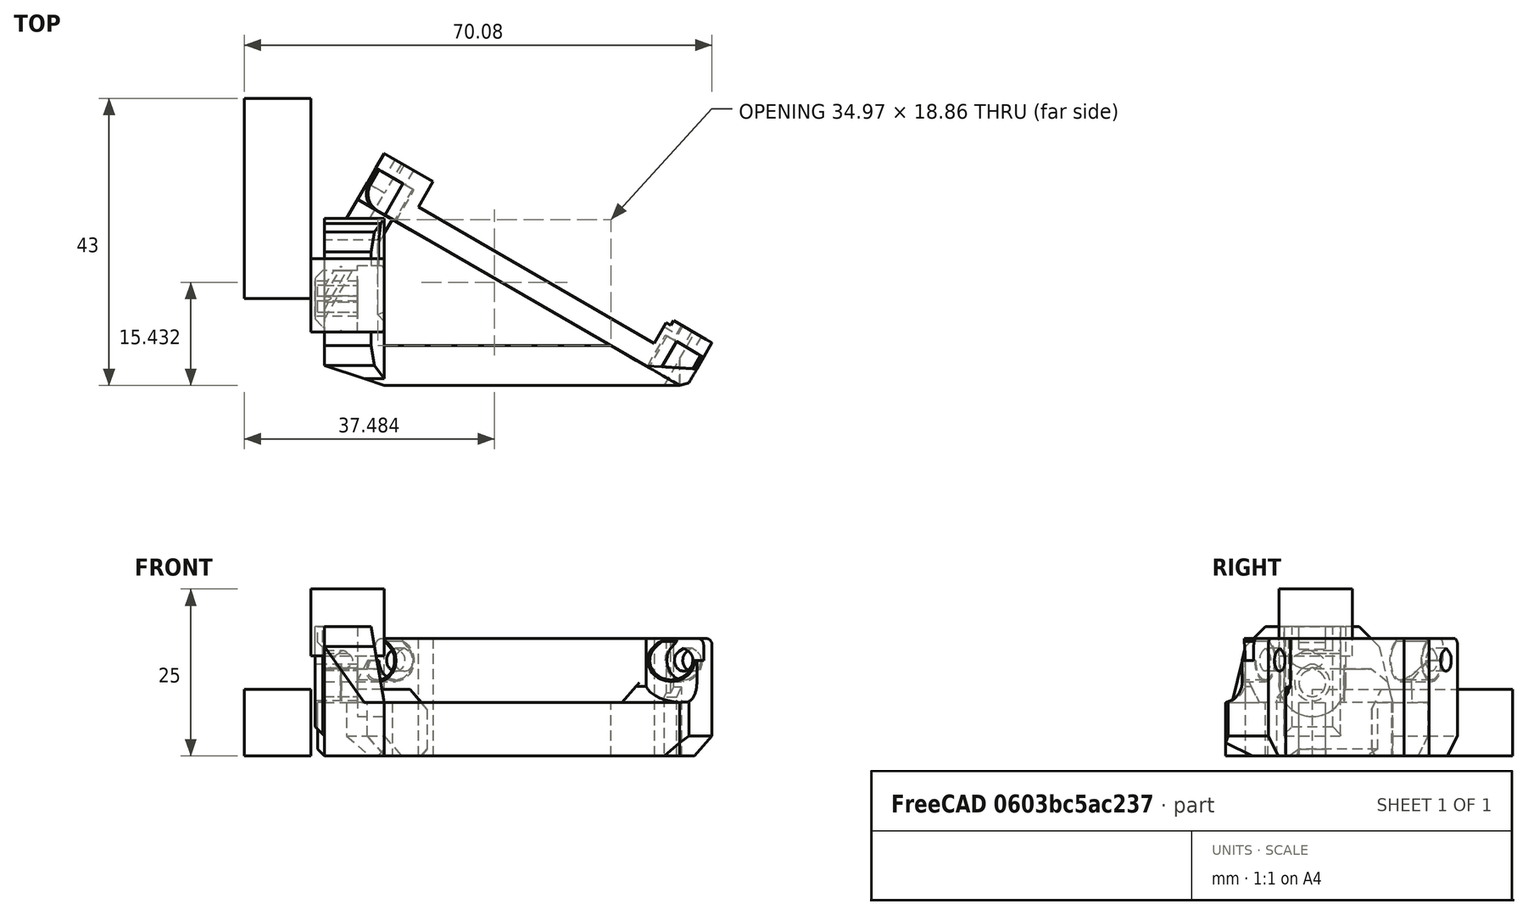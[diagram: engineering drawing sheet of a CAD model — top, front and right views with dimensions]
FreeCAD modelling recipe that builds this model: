
FCSTD DOCUMENT  (FreeCAD 0.18R14555 (Git shallow))
Label: lcd-mount
License: All rights reserved
LicenseURL: http://en.wikipedia.org/wiki/All_rights_reserved
objects: Part::Box×12, Part::Cut×10, Part::Feature×7, Part::Chamfer×5, Part::MultiFuse×4, Part::Cylinder×4, Part::MultiCommon×1
note: 43 computed .brp shape members not serialized (recipe doc carries the construction recipe); baked Part::Feature solids carry a one-line shape summary decoded from their .brp

FEATURE [Part::Feature] Part__Feature  label="lcd_support_a v22"
  Placement = pos=(0,0,8) rot=(0,0,1;0rad)
  shape: bbox 50.99 x 46.14 x 19.4 mm, 94 faces (baked)
FEATURE [Part::Box] Box  label="Cube"
  AttacherType = Attacher::AttachEngine3D
  Height = 23
  Length = 68
  Placement = pos=(-21.0205,17.607,0) rot=(0,0,-1;0.785398rad)
  Width = 33
FEATURE [Part::Feature] Part__Feature001  label="lcd_support_a v023"
  Placement = pos=(0,0,8) rot=(0,0,1;0rad)
  shape: bbox 50.99 x 46.14 x 19.4 mm, 94 faces (baked)
FEATURE [Part::Cut] Cut
  Base = -> Part__Feature
  Placement = pos=(2.45,-11.18,0) rot=(0,0,1;0.261799rad)
  Tool = -> Box
FEATURE [Part::Box] Box002  label="Cube002"
  AttacherType = Attacher::AttachEngine3D
  Height = 20
  Length = 11
  Placement = pos=(-2,0,0) rot=(0,0,1;0rad)
  Width = 26
FEATURE [Part::MultiCommon] Common
  Placement = pos=(-9,0,0) rot=(0,0,1;0rad)
  Shapes = -> [Part__Feature001,Box002]
FEATURE [Part::Box] Box004  label="Cube004"
  AttacherType = Attacher::AttachEngine3D
  Height = 8
  Length = 44.24
  Width = 6
FEATURE [Part::Box] Box006  label="Cube006"
  AttacherType = Attacher::AttachEngine3D
  Height = 10
  Length = 10
  Placement = pos=(-9,25,0) rot=(0,0,1;0rad)
  Width = 10
FEATURE [Part::Cut] Cut001
  Base = -> Common
  Tool = -> Box006
FEATURE [Part::Box] Box012  label="Cube012"
  AttacherType = Attacher::AttachEngine3D
  Height = 10
  Length = 10
  Width = 10
FEATURE [Part::Box] Box013  label="Cube013"
  AttacherType = Attacher::AttachEngine3D
  Height = 10
  Length = 10
  Width = 10
FEATURE [Part::Chamfer] Chamfer
  Base = -> Box012
  Edges = 1 edges r=4: [Edge8]
FEATURE [Part::Cut] Cut004  label="corner-cut"
  Base = -> Box013
  Placement = pos=(34.86,-0.255514,0) rot=(0,0,-1;0.523599rad)
  Tool = -> Chamfer
FEATURE [Part::Box] Box014  label="Cube014"
  AttacherType = Attacher::AttachEngine3D
  Height = 10
  Length = 10
  Placement = pos=(-21,13,0) rot=(0,0,1;0rad)
  Width = 30
FEATURE [Part::Box] Box015  label="Cube015"
  AttacherType = Attacher::AttachEngine3D
  Height = 8
  Length = 7
  Placement = pos=(-0.87269,21.2885,0) rot=(0,0,1;1.0472rad)
  Width = 6
FEATURE [Part::Chamfer] Chamfer001
  Base = -> Box015
  Edges = 1 edges r=3: [Edge11]
FEATURE [Part::Cut] Cut005
  Base = -> Box004
  Tool = -> Cut004
FEATURE [Part::MultiFuse] Fusion
  Shapes = -> [Cut005,Chamfer001,Cut001,Cut]
FEATURE [Part::Feature] Fusion001
  shape: bbox 59.48 x 34.88 x 19.4 mm, 97 faces (baked)
FEATURE [Part::Cylinder] Cylinder
  Angle = 360
  AttacherType = Attacher::AttachEngine3D
  Height = 6
  Placement = pos=(-1.29105,25.6638,14.3) rot=(-0.447214,0.774597,0.447214;1.82348rad)
  Radius = 3.15
FEATURE [Part::Box] Box016  label="Cube016"
  AttacherType = Attacher::AttachEngine3D
  Height = 10
  Length = 11
  Placement = pos=(-11,8,15) rot=(0,0,1;0rad)
  Width = 11
FEATURE [Part::Box] Box017  label="Cube017"
  AttacherType = Attacher::AttachEngine3D
  Height = 10
  Length = 11
  Placement = pos=(-11,17.23,13) rot=(0,0,1;0rad)
  Width = 8
FEATURE [Part::Cylinder] Cylinder001
  Angle = 360
  AttacherType = Attacher::AttachEngine3D
  Height = 10
  Placement = pos=(39.837,-2.70027,14.3) rot=(-0.447214,0.774597,0.447214;1.82348rad)
  Radius = 3.15
FEATURE [Part::Cut] Cut006
  Base = -> Fusion001
  Tool = -> Cylinder
FEATURE [Part::Cut] Cut007
  Base = -> Cut006
  Tool = -> Cylinder001
FEATURE [Part::Cut] Cut008
  Base = -> Cut007
  Tool = -> Box017
FEATURE [Part::Chamfer] Chamfer002
  Base = -> Cut008
  Edges = 1 edges r=2: [Edge154]
FEATURE [Part::Cylinder] Cylinder003
  Angle = 360
  AttacherType = Attacher::AttachEngine3D
  Height = 33
  Placement = pos=(-15.2911,1.41512,14.3) rot=(-0.447214,0.774597,0.447214;1.82348rad)
  Radius = 1.2
FEATURE [Part::Cylinder] Cylinder004
  Angle = 360
  AttacherType = Attacher::AttachEngine3D
  Height = 33
  Placement = pos=(-15.2911,1.41512,15.3) rot=(-0.447214,0.774597,0.447214;1.82348rad)
  Radius = 0.5
FEATURE [Part::Feature] Part__Feature003  label="m5-to-m4-bolt-hole"
  Placement = pos=(-4,13,10.9) rot=(0,0,-1;1.5708rad)
  shape: bbox 3 x 6 x 6 mm, 5 faces (baked)
FEATURE [Part::Feature] Part__Feature004  label="m5-to-m4-bolt-hole001"
  Placement = pos=(-7,13,10.9) rot=(0,0,-1;1.5708rad)
  shape: bbox 3 x 6 x 6 mm, 5 faces (baked)
FEATURE [Part::MultiFuse] Fusion002
  Shapes = -> [Part__Feature004,Part__Feature003,Chamfer002]
FEATURE [Part::MultiFuse] Fusion003
  Shapes = -> [Cylinder003,Cylinder004]
FEATURE [Part::Cut] Cut009
  Base = -> Fusion002
  Tool = -> Fusion003
FEATURE [Part::Box] Box018  label="Cube018"
  AttacherType = Attacher::AttachEngine3D
  Height = 9
  Length = 2
  Placement = pos=(-15,0,8) rot=(0,0,1;0rad)
  Width = 19
FEATURE [Part::Chamfer] Chamfer003
  Base = -> Box018
  Edges = 1 edges r=1: [Edge6]
  Placement = pos=(4,0,0) rot=(0,0,1;0rad)
FEATURE [Part::Feature] Part__Feature005  label="t-slot-align"
  Placement = pos=(-9,18.23,-2e-15) rot=(-0.57735,0.57735,-0.57735;4.18879rad)
  shape: bbox 5 x 10.45 x 60 mm, 10 faces (baked)
FEATURE [Part::Cut] Cut010
  Base = -> Cut009
  Tool = -> Part__Feature005
FEATURE [Part::Box] Box019  label="Cube019"
  AttacherType = Attacher::AttachEngine3D
  Height = 5
  Length = 2
  Placement = pos=(-10,11.01,0) rot=(0,0,1;0rad)
  Width = 4
FEATURE [Part::Chamfer] Chamfer004
  Base = -> Box019
  Edges = 1 edges r=1: [Edge4]
  Placement = pos=(0,-0.005,0) rot=(0,0,1;0rad)
FEATURE [Part::MultiFuse] Fusion004
  Shapes = -> [Cut010,Chamfer004]
FEATURE [Part::Cut] Cut011
  Base = -> Fusion004
  Tool = -> Chamfer003
FEATURE [Part::Feature] Cut011001  label="Cut012"
  shape: bbox 60.16 x 34.96 x 19.4 mm, 105 faces (baked)
